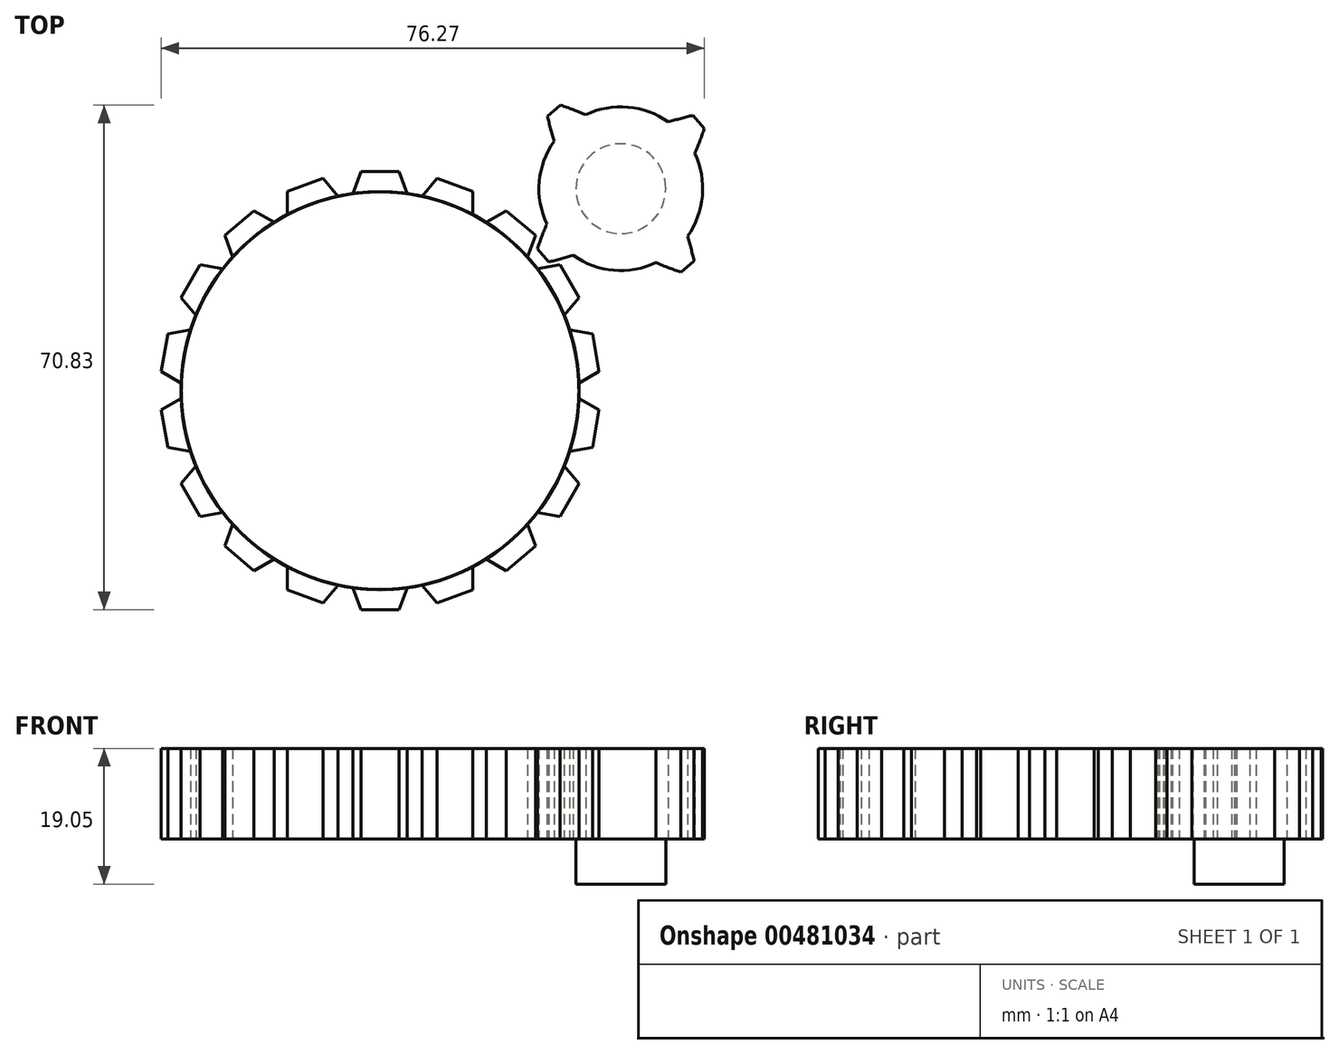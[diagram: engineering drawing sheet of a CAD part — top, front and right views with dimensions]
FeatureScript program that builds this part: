
annotation { "Feature Type Name" : "Feature", "Feature Type Description" : "" }
export const myFeature = defineFeature(function(context is Context, id is Id, definition is map)
    precondition{}
    {
        {
            var Q0;
            Q0=qCreatedBy(makeId("Top.planeOp"),FACE);
            var sketch = newSketch(context, id + "F0", { "sketchPlane" : qUnion([Q0])});
            skCircle(sketch, "E0", {"center": v(0, 0) * mm, "radius": 30.86 * mm, "construction": true});
            skCircle(sketch, "E1", {"center": v(0, 0) * mm, "radius": 38.1 * mm, "construction": true});
            skCircle(sketch, "E2", {"center": v(0, 0) * mm, "radius": 27.94 * mm});
            skLineSegment(sketch, "E3", {"start": v(0, 0) * mm, "end": v(0, 55.14) * mm, "construction": true});
            skCircle(sketch, "E4", {"center": v(0, 30.86) * mm, "radius": 8.9 * mm, "construction": true});
            skLineSegment(sketch, "E5", {"start": v(0, 38.1) * mm, "end": v(-70.67, 38.1) * mm, "construction": true});
            skLineSegment(sketch, "E6", {"start": v(0, 38.1) * mm, "end": v(-13.87, 0) * mm, "construction": true});
            skLineSegment(sketch, "E7", {"start": v(0, 38.1) * mm, "end": v(13.87, 0) * mm, "construction": true});
            skFitSpline(sketch, "E8", {"points": [v(-3.8, 27.68) * mm, v(-2.68, 30.74) * mm], "startDerivative": vector(1.11, 3.06) * mm, "endDerivative": vector(1.11, 3.06) * mm});
            skFitSpline(sketch, "E9", {"points": [v(-2.68, 30.74) * mm, v(2.68, 30.74) * mm], "startDerivative": vector(5.35, 0) * mm, "endDerivative": vector(5.35, 0) * mm});
            skFitSpline(sketch, "E10", {"points": [v(2.68, 30.74) * mm, v(3.8, 27.68) * mm, v(3.86, 27.5) * mm], "startDerivative": vector(1.8, -4.97) * mm, "endDerivative": vector(0.24, -0.65) * mm});
            skSolve(sketch);
        }
        {
            var Q0;
            Q0 = qSketchRegion(id + "F0", true);
            extrude(context, id + "F1", {"entities" : qUnion([Q0]), "depth" : 12.7 * mm});
        }
        {
            var Q0;
            Q0=makeQuery(id+"F1.opExtrude","SWEPT_BODY",BODY,{"disambiguationData":[OSD([sQuery(id+"F0.wireOp",EDGE,"E2"),sQuery(id+"F0.wireOp",EDGE,"E8"),sQuery(id+"F0.wireOp",EDGE,"E9"),sQuery(id+"F0.wireOp",EDGE,"E10")])]});
            var Q1;
            Q1=makeQuery(id+"F1.opExtrude","SWEPT_FACE",FACE,{"disambiguationData":[OSD([sQuery(id+"F0.wireOp",EDGE,"E2")])]});
            circularPattern(context, id + "F2", {"entities" : qUnion([Q0]), "axis" : qUnion([Q1]), "angle" : 360 * degree, "instanceCount" : 18, "equalSpace" : true});
        }
        {
            var Q0;
            Q0=qCreatedBy(makeId("Top.planeOp"),FACE);
            var sketch = newSketch(context, id + "F3", { "sketchPlane" : qUnion([Q0])});
            skLineSegment(sketch, "E11", {"start": v(30.75, 2.7) * mm, "end": v(30.75, -2.72) * mm, "construction": true});
            skLineSegment(sketch, "E12", {"start": v(0, 27.91) * mm, "end": v(28.28, 27.91) * mm, "construction": true});
            skLineSegment(sketch, "E13", {"start": v(0, 0) * mm, "end": v(33.8, 28.36) * mm, "construction": true});
            skCircle(sketch, "E14", {"center": v(33.8, 28.36) * mm, "radius": 14.45 * mm, "construction": true});
            skCircle(sketch, "E15", {"center": v(33.8, 28.36) * mm, "radius": 18.37 * mm, "construction": true});
            skCircle(sketch, "E16", {"center": v(33.8, 28.36) * mm, "radius": 11.5 * mm});
            skLineSegment(sketch, "E17", {"start": v(0, 0) * mm, "end": v(33.16, 33.16) * mm, "construction": true});
            skLineSegment(sketch, "E18", {"start": v(0, 0) * mm, "end": v(39.77, 27.85) * mm, "construction": true});
            skArc(sketch, "E19", {"start": v(23.42, 23.42) * mm, "mid": v(22.7, 21.68) * mm, "end": v(22.07, 19.9) * mm});
            skArc(sketch, "E20", {"start": v(23.65, 18.07) * mm, "mid": v(25.4, 18.5) * mm, "end": v(27.13, 19) * mm});
            skLineSegment(sketch, "E21", {"start": v(22.07, 19.9) * mm, "end": v(23.65, 18.07) * mm});
            skSolve(sketch);
        }
        {
            var Q0;
            Q0 = qSketchRegion(id + "F3", true);
            extrude(context, id + "F4", {"entities" : qUnion([Q0]), "depth" : 12.7 * mm});
        }
        {
            var Q0;
            Q0=makeQuery(id+"F4.opExtrude","SWEPT_BODY",BODY,{"disambiguationData":[OSD([sQuery(id+"F3.wireOp",EDGE,"E16"),sQuery(id+"F3.wireOp",EDGE,"E19"),sQuery(id+"F3.wireOp",EDGE,"E20"),sQuery(id+"F3.wireOp",EDGE,"E21")])]});
            var Q1;
            Q1=makeQuery(id+"F4.opExtrude","SWEPT_FACE",FACE,{"disambiguationData":[OSD([sQuery(id+"F3.wireOp",EDGE,"E16")])]});
            circularPattern(context, id + "F5", {"entities" : qUnion([Q0]), "axis" : qUnion([Q1]), "angle" : 360 * degree, "instanceCount" : 4, "equalSpace" : true});
        }
        {
            var Q0;
            Q0=makeQuery(id+"F5.opPattern","COPY",BODY,{"derivedFrom":makeQuery(id+"F4.opExtrude","SWEPT_BODY",BODY,{"disambiguationData":[OSD([sQuery(id+"F3.wireOp",EDGE,"E16"),sQuery(id+"F3.wireOp",EDGE,"E19"),sQuery(id+"F3.wireOp",EDGE,"E20"),sQuery(id+"F3.wireOp",EDGE,"E21")])]}),"instanceName":"1"});
            var Q1;
            Q1=makeQuery(id+"F5.opPattern","COPY",BODY,{"derivedFrom":makeQuery(id+"F4.opExtrude","SWEPT_BODY",BODY,{"disambiguationData":[OSD([sQuery(id+"F3.wireOp",EDGE,"E16"),sQuery(id+"F3.wireOp",EDGE,"E19"),sQuery(id+"F3.wireOp",EDGE,"E20"),sQuery(id+"F3.wireOp",EDGE,"E21")])]}),"instanceName":"3"});
            var Q2;
            Q2=makeQuery(id+"F5.opPattern","COPY",BODY,{"derivedFrom":makeQuery(id+"F4.opExtrude","SWEPT_BODY",BODY,{"disambiguationData":[OSD([sQuery(id+"F3.wireOp",EDGE,"E16"),sQuery(id+"F3.wireOp",EDGE,"E19"),sQuery(id+"F3.wireOp",EDGE,"E20"),sQuery(id+"F3.wireOp",EDGE,"E21")])]}),"instanceName":"2"});
            var Q3;
            Q3=makeQuery(id+"F4.opExtrude","SWEPT_BODY",BODY,{"disambiguationData":[OSD([sQuery(id+"F3.wireOp",EDGE,"E16"),sQuery(id+"F3.wireOp",EDGE,"E19"),sQuery(id+"F3.wireOp",EDGE,"E20"),sQuery(id+"F3.wireOp",EDGE,"E21")])]});
            booleanBodies(context, id + "F6", {"operationType" : BooleanOperationType.UNION, "tools" : qUnion([Q0, Q1, Q2, Q3])});
        }
        {
            var Q0;
            {var subQ0=makeQuery(id+"F4.opExtrude","CAP_FACE",FACE,{"disambiguationData":[OSD([sQuery(id+"F3.wireOp",EDGE,"E16"),sQuery(id+"F3.wireOp",EDGE,"E19"),sQuery(id+"F3.wireOp",EDGE,"E20"),sQuery(id+"F3.wireOp",EDGE,"E21")])],"isStart":true});Q0=makeQuery(id+"F6.opBoolean","MERGE",FACE,{"derivedFrom":[subQ0,makeQuery(id+"F5.opPattern","COPY",FACE,{"derivedFrom":subQ0,"instanceName":"1"}),makeQuery(id+"F5.opPattern","COPY",FACE,{"derivedFrom":subQ0,"instanceName":"2"}),makeQuery(id+"F5.opPattern","COPY",FACE,{"derivedFrom":subQ0,"instanceName":"3"})]});}
            var sketch = newSketch(context, id + "F7", { "sketchPlane" : qUnion([Q0])});
            skCircle(sketch, "E22", {"center": v(33.8, -28.36) * mm, "radius": 6.3 * mm});
            skSolve(sketch);
        }
        {
            var Q0;
            Q0 = qSketchRegion(id + "F7", true);
            extrude(context, id + "F8", {"entities" : qUnion([Q0]), "operationType" : NewBodyOperationType.ADD, "depth" : 6.35 * mm});
        }
    });
